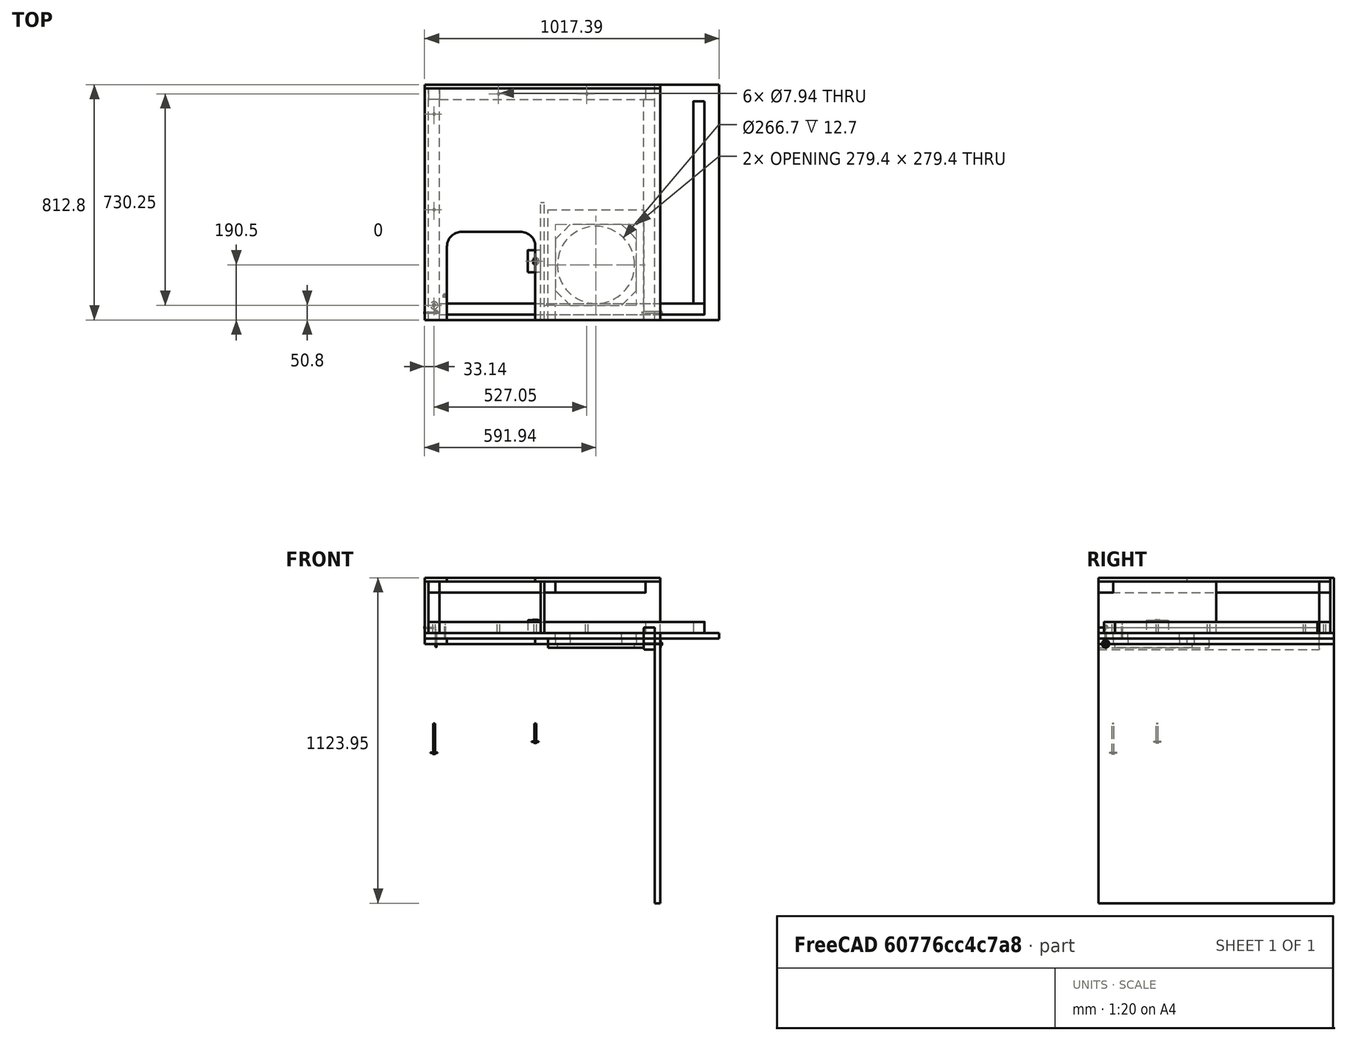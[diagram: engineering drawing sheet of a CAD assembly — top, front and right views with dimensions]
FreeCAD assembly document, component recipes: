
FREECAD ASSEMBLY — COMPONENT RECIPES ("Assembly")

This assembly document has 114 components, labeled P0..P113 below (a component is one placed body or linked part). 0 of them carry a construction recipe — the FreeCAD feature program that regenerates the part from scratch, quoted from this document or its linked companion documents; the rest are supplied as boundary geometry only. No exploded tour is included for this assembly.
COMPONENT P0 — geometry summary ("IF_A001"; no construction recipe available for this part):
  bounding box: 762.0 x 38.1 x 38.1 mm
  tessellated surface: 108 triangles
  volume: 1099533 mm^3 (99% of its bounding box)
  symmetry: 2-fold rotationally symmetric about the x axis; 4-fold rotationally symmetric about the y axis; 2-fold rotationally symmetric about the z axis; mirror-symmetric across its x mid-plane, z mid-plane
COMPONENT P1 — geometry summary ("Screw_w_Washer_B006"; no construction recipe available for this part):
  bounding box: 50.8 x 15.9 x 15.8 mm
  tessellated surface: 1,084 triangles
  volume: 650 mm^3 (5% of its bounding box)
  symmetry: 4-fold rotationally symmetric about the z axis; mirror-symmetric across its x mid-plane, y mid-plane
COMPONENT P2 — geometry summary ("Screw_w_Washer_B007"; no construction recipe available for this part):
  bounding box: 50.8 x 15.9 x 15.8 mm
  tessellated surface: 1,084 triangles
  volume: 650 mm^3 (5% of its bounding box)
  symmetry: 4-fold rotationally symmetric about the z axis; mirror-symmetric across its x mid-plane, y mid-plane
COMPONENT P3 — geometry summary ("Screw_w_Washer_B008"; no construction recipe available for this part):
  bounding box: 50.8 x 15.9 x 15.8 mm
  tessellated surface: 1,084 triangles
  volume: 650 mm^3 (5% of its bounding box)
  symmetry: 4-fold rotationally symmetric about the z axis; mirror-symmetric across its x mid-plane, y mid-plane
COMPONENT P4 — geometry summary ("Screw_w_Washer_B009"; no construction recipe available for this part):
  bounding box: 50.8 x 15.9 x 15.8 mm
  tessellated surface: 1,084 triangles
  volume: 650 mm^3 (5% of its bounding box)
  symmetry: 4-fold rotationally symmetric about the z axis; mirror-symmetric across its x mid-plane, y mid-plane
COMPONENT P5 — geometry summary ("Screw_w_Washer_B010"; no construction recipe available for this part):
  bounding box: 50.8 x 15.9 x 15.8 mm
  tessellated surface: 1,084 triangles
  volume: 650 mm^3 (5% of its bounding box)
  symmetry: 4-fold rotationally symmetric about the z axis; mirror-symmetric across its x mid-plane, y mid-plane
COMPONENT P6 — geometry summary ("Screw_w_Washer_B011"; no construction recipe available for this part):
  bounding box: 50.8 x 15.9 x 15.8 mm
  tessellated surface: 1,084 triangles
  volume: 650 mm^3 (5% of its bounding box)
  symmetry: 4-fold rotationally symmetric about the z axis; mirror-symmetric across its x mid-plane, y mid-plane
COMPONENT P7 — geometry summary ("Screw_w_Washer_B012"; no construction recipe available for this part):
  bounding box: 50.8 x 15.9 x 15.8 mm
  tessellated surface: 1,084 triangles
  volume: 650 mm^3 (5% of its bounding box)
  symmetry: 4-fold rotationally symmetric about the z axis; mirror-symmetric across its x mid-plane, y mid-plane
COMPONENT P8 — geometry summary ("Screw_w_Washer_B013"; no construction recipe available for this part):
  bounding box: 50.8 x 15.9 x 15.8 mm
  tessellated surface: 1,084 triangles
  volume: 650 mm^3 (5% of its bounding box)
  symmetry: 4-fold rotationally symmetric about the z axis; mirror-symmetric across its x mid-plane, y mid-plane
COMPONENT P9 — geometry summary ("Screw_w_Washer_B014"; no construction recipe available for this part):
  bounding box: 50.8 x 15.9 x 15.8 mm
  tessellated surface: 1,084 triangles
  volume: 650 mm^3 (5% of its bounding box)
  symmetry: 4-fold rotationally symmetric about the z axis; mirror-symmetric across its x mid-plane, y mid-plane
COMPONENT P10 — geometry summary ("Screw_w_Washer_B015"; no construction recipe available for this part):
  bounding box: 50.8 x 15.9 x 15.8 mm
  tessellated surface: 1,084 triangles
  volume: 650 mm^3 (5% of its bounding box)
  symmetry: 4-fold rotationally symmetric about the z axis; mirror-symmetric across its x mid-plane, y mid-plane
COMPONENT P11 — geometry summary ("Screw_w_Washer_B016"; no construction recipe available for this part):
  bounding box: 50.8 x 15.9 x 15.8 mm
  tessellated surface: 1,084 triangles
  volume: 650 mm^3 (5% of its bounding box)
  symmetry: 4-fold rotationally symmetric about the z axis; mirror-symmetric across its x mid-plane, y mid-plane
COMPONENT P12 — geometry summary ("Screw_w_Washer_B017"; no construction recipe available for this part):
  bounding box: 50.8 x 15.9 x 15.8 mm
  tessellated surface: 1,084 triangles
  volume: 650 mm^3 (5% of its bounding box)
  symmetry: 4-fold rotationally symmetric about the z axis; mirror-symmetric across its x mid-plane, y mid-plane
COMPONENT P13 — geometry summary ("Screw_w_Washer_B018"; no construction recipe available for this part):
  bounding box: 50.8 x 15.9 x 15.8 mm
  tessellated surface: 1,084 triangles
  volume: 650 mm^3 (5% of its bounding box)
  symmetry: 4-fold rotationally symmetric about the z axis; mirror-symmetric across its x mid-plane, y mid-plane
COMPONENT P14 — geometry summary ("Screw_w_Washer_B019"; no construction recipe available for this part):
  bounding box: 50.8 x 15.9 x 15.8 mm
  tessellated surface: 1,084 triangles
  volume: 650 mm^3 (5% of its bounding box)
  symmetry: 4-fold rotationally symmetric about the z axis; mirror-symmetric across its x mid-plane, y mid-plane
COMPONENT P15 — geometry summary ("Part_F_Baffle_Side_Wall_002"; no construction recipe available for this part):
  bounding box: 800.1 x 177.8 x 12.7 mm
  tessellated surface: 12 triangles
  volume: 1806674 mm^3 (100% of its bounding box)
  symmetry: 2-fold rotationally symmetric about the x axis; 2-fold rotationally symmetric about the y axis; 2-fold rotationally symmetric about the z axis; mirror-symmetric across its x mid-plane, y mid-plane, z mid-plane
COMPONENT P16 — geometry summary ("BF_A001"; no construction recipe available for this part):
  bounding box: 800.1 x 38.1 x 38.1 mm
  tessellated surface: 108 triangles
  volume: 1154510 mm^3 (99% of its bounding box)
  symmetry: 2-fold rotationally symmetric about the x axis; 4-fold rotationally symmetric about the y axis; 2-fold rotationally symmetric about the z axis; mirror-symmetric across its x mid-plane, z mid-plane
COMPONENT P17 — geometry summary ("BF_B001"; no construction recipe available for this part):
  bounding box: 711.2 x 38.1 x 38.1 mm
  tessellated surface: 108 triangles
  volume: 1026231 mm^3 (99% of its bounding box)
  symmetry: 2-fold rotationally symmetric about the x axis; 2-fold rotationally symmetric about the y axis; 2-fold rotationally symmetric about the z axis; mirror-symmetric across its y mid-plane, z mid-plane
COMPONENT P18 — geometry summary ("BF_C001"; no construction recipe available for this part):
  bounding box: 139.7 x 38.1 x 38.1 mm
  tessellated surface: 108 triangles
  volume: 201581 mm^3 (99% of its bounding box)
  symmetry: 2-fold rotationally symmetric about the y axis; 4-fold rotationally symmetric about the z axis; mirror-symmetric across its x mid-plane, y mid-plane, z mid-plane
COMPONENT P19 — geometry summary ("BF_E001"; no construction recipe available for this part):
  bounding box: 50.8 x 38.1 x 38.1 mm
  tessellated surface: 108 triangles
  volume: 73302 mm^3 (99% of its bounding box)
  symmetry: 2-fold rotationally symmetric about the x axis; 2-fold rotationally symmetric about the y axis; 2-fold rotationally symmetric about the z axis
COMPONENT P20 — geometry summary ("Screw_w_Washer_A001"; no construction recipe available for this part):
  bounding box: 38.1 x 15.9 x 15.8 mm
  tessellated surface: 1,086 triangles
  volume: 527 mm^3 (5% of its bounding box)
  symmetry: 4-fold rotationally symmetric about the x axis; mirror-symmetric across its y mid-plane
COMPONENT P21 — geometry summary ("Screw_w_Washer_A002"; no construction recipe available for this part):
  bounding box: 38.1 x 15.9 x 15.8 mm
  tessellated surface: 1,086 triangles
  volume: 527 mm^3 (5% of its bounding box)
  symmetry: 4-fold rotationally symmetric about the x axis; mirror-symmetric across its y mid-plane
COMPONENT P22 — geometry summary ("Screw_w_Washer_A003"; no construction recipe available for this part):
  bounding box: 38.1 x 15.9 x 15.8 mm
  tessellated surface: 1,086 triangles
  volume: 527 mm^3 (5% of its bounding box)
  symmetry: 4-fold rotationally symmetric about the x axis; mirror-symmetric across its y mid-plane
COMPONENT P23 — geometry summary ("Screw_w_Washer_A004"; no construction recipe available for this part):
  bounding box: 38.1 x 15.9 x 15.8 mm
  tessellated surface: 1,086 triangles
  volume: 527 mm^3 (5% of its bounding box)
  symmetry: 4-fold rotationally symmetric about the x axis; mirror-symmetric across its y mid-plane
COMPONENT P24 — geometry summary ("Screw_w_Washer_A005"; no construction recipe available for this part):
  bounding box: 38.1 x 15.9 x 15.8 mm
  tessellated surface: 1,086 triangles
  volume: 527 mm^3 (5% of its bounding box)
  symmetry: 4-fold rotationally symmetric about the x axis; mirror-symmetric across its y mid-plane
COMPONENT P25 — geometry summary ("Screw_w_Washer_A006"; no construction recipe available for this part):
  bounding box: 38.1 x 15.9 x 15.8 mm
  tessellated surface: 1,086 triangles
  volume: 527 mm^3 (5% of its bounding box)
  symmetry: 4-fold rotationally symmetric about the x axis; mirror-symmetric across its y mid-plane
COMPONENT P26 — geometry summary ("Screw_w_Washer_A007"; no construction recipe available for this part):
  bounding box: 38.1 x 15.9 x 15.8 mm
  tessellated surface: 1,086 triangles
  volume: 527 mm^3 (5% of its bounding box)
  symmetry: 4-fold rotationally symmetric about the x axis; mirror-symmetric across its y mid-plane
COMPONENT P27 — geometry summary ("Screw_w_Washer_A008"; no construction recipe available for this part):
  bounding box: 38.1 x 15.9 x 15.8 mm
  tessellated surface: 1,086 triangles
  volume: 527 mm^3 (5% of its bounding box)
  symmetry: 4-fold rotationally symmetric about the x axis; mirror-symmetric across its y mid-plane
COMPONENT P28 — geometry summary ("Screw_w_Washer_A009"; no construction recipe available for this part):
  bounding box: 38.1 x 15.9 x 15.8 mm
  tessellated surface: 1,086 triangles
  volume: 527 mm^3 (5% of its bounding box)
  symmetry: 4-fold rotationally symmetric about the x axis; mirror-symmetric across its y mid-plane
COMPONENT P29 — geometry summary ("Screw_w_Washer_A010"; no construction recipe available for this part):
  bounding box: 38.1 x 15.9 x 15.8 mm
  tessellated surface: 1,086 triangles
  volume: 527 mm^3 (5% of its bounding box)
  symmetry: 4-fold rotationally symmetric about the x axis; mirror-symmetric across its y mid-plane
COMPONENT P30 — geometry summary ("Screw_w_Washer_A011"; no construction recipe available for this part):
  bounding box: 38.1 x 15.9 x 15.8 mm
  tessellated surface: 1,086 triangles
  volume: 527 mm^3 (5% of its bounding box)
  symmetry: 4-fold rotationally symmetric about the x axis; mirror-symmetric across its y mid-plane
COMPONENT P31 — geometry summary ("Screw_w_Washer_A012"; no construction recipe available for this part):
  bounding box: 38.1 x 15.9 x 15.8 mm
  tessellated surface: 1,086 triangles
  volume: 527 mm^3 (5% of its bounding box)
  symmetry: 4-fold rotationally symmetric about the x axis; mirror-symmetric across its y mid-plane
COMPONENT P32 — geometry summary ("Screw_w_Washer_A013"; no construction recipe available for this part):
  bounding box: 38.1 x 15.9 x 15.8 mm
  tessellated surface: 1,086 triangles
  volume: 527 mm^3 (5% of its bounding box)
  symmetry: 4-fold rotationally symmetric about the x axis; mirror-symmetric across its y mid-plane
COMPONENT P33 — geometry summary ("Screw_w_Washer_A014"; no construction recipe available for this part):
  bounding box: 38.1 x 15.9 x 15.8 mm
  tessellated surface: 1,086 triangles
  volume: 527 mm^3 (5% of its bounding box)
  symmetry: 4-fold rotationally symmetric about the x axis; mirror-symmetric across its y mid-plane
COMPONENT P34 — geometry summary ("Screw_w_Washer_A015"; no construction recipe available for this part):
  bounding box: 38.1 x 15.9 x 15.8 mm
  tessellated surface: 1,086 triangles
  volume: 527 mm^3 (5% of its bounding box)
  symmetry: 4-fold rotationally symmetric about the x axis; mirror-symmetric across its y mid-plane
COMPONENT P35 — geometry summary ("Screw_w_Washer_A016"; no construction recipe available for this part):
  bounding box: 38.1 x 15.9 x 15.8 mm
  tessellated surface: 1,086 triangles
  volume: 527 mm^3 (5% of its bounding box)
  symmetry: 4-fold rotationally symmetric about the x axis; mirror-symmetric across its y mid-plane
COMPONENT P36 — geometry summary ("Screw_w_Washer_A017"; no construction recipe available for this part):
  bounding box: 38.1 x 15.9 x 15.8 mm
  tessellated surface: 1,086 triangles
  volume: 527 mm^3 (5% of its bounding box)
  symmetry: 4-fold rotationally symmetric about the x axis; mirror-symmetric across its y mid-plane
COMPONENT P37 — geometry summary ("Screw_w_Washer_A018"; no construction recipe available for this part):
  bounding box: 38.1 x 15.9 x 15.8 mm
  tessellated surface: 1,086 triangles
  volume: 527 mm^3 (5% of its bounding box)
  symmetry: 4-fold rotationally symmetric about the x axis; mirror-symmetric across its y mid-plane
COMPONENT P38 — geometry summary ("Screw_w_Washer_A019"; no construction recipe available for this part):
  bounding box: 38.1 x 15.9 x 15.8 mm
  tessellated surface: 1,086 triangles
  volume: 527 mm^3 (5% of its bounding box)
  symmetry: 4-fold rotationally symmetric about the x axis; mirror-symmetric across its y mid-plane
COMPONENT P39 — geometry summary ("Screw_w_Washer_A020"; no construction recipe available for this part):
  bounding box: 38.1 x 15.9 x 15.8 mm
  tessellated surface: 1,086 triangles
  volume: 527 mm^3 (5% of its bounding box)
  symmetry: 4-fold rotationally symmetric about the x axis; mirror-symmetric across its y mid-plane
COMPONENT P40 — geometry summary ("Screw_w_Washer_A021"; no construction recipe available for this part):
  bounding box: 38.1 x 15.9 x 15.8 mm
  tessellated surface: 1,086 triangles
  volume: 527 mm^3 (5% of its bounding box)
  symmetry: 4-fold rotationally symmetric about the x axis; mirror-symmetric across its y mid-plane
COMPONENT P41 — geometry summary ("Screw_w_Washer_A022"; no construction recipe available for this part):
  bounding box: 38.1 x 15.9 x 15.8 mm
  tessellated surface: 1,086 triangles
  volume: 527 mm^3 (5% of its bounding box)
  symmetry: 4-fold rotationally symmetric about the x axis; mirror-symmetric across its y mid-plane
COMPONENT P42 — geometry summary ("Screw_w_Washer_A023"; no construction recipe available for this part):
  bounding box: 38.1 x 15.9 x 15.8 mm
  tessellated surface: 1,086 triangles
  volume: 527 mm^3 (5% of its bounding box)
  symmetry: 4-fold rotationally symmetric about the x axis; mirror-symmetric across its y mid-plane
COMPONENT P43 — geometry summary ("Screw_w_Washer_A024"; no construction recipe available for this part):
  bounding box: 38.1 x 15.9 x 15.8 mm
  tessellated surface: 1,086 triangles
  volume: 527 mm^3 (5% of its bounding box)
  symmetry: 4-fold rotationally symmetric about the x axis; mirror-symmetric across its y mid-plane
COMPONENT P44 — geometry summary ("Screw_w_Washer_A025"; no construction recipe available for this part):
  bounding box: 38.1 x 15.9 x 15.8 mm
  tessellated surface: 1,086 triangles
  volume: 527 mm^3 (5% of its bounding box)
  symmetry: 4-fold rotationally symmetric about the x axis; mirror-symmetric across its y mid-plane
COMPONENT P45 — geometry summary ("Screw_w_Washer_A026"; no construction recipe available for this part):
  bounding box: 38.1 x 15.9 x 15.8 mm
  tessellated surface: 1,086 triangles
  volume: 527 mm^3 (5% of its bounding box)
  symmetry: 4-fold rotationally symmetric about the x axis; mirror-symmetric across its y mid-plane
COMPONENT P46 — geometry summary ("Screw_w_Washer_A027"; no construction recipe available for this part):
  bounding box: 38.1 x 15.9 x 15.8 mm
  tessellated surface: 1,086 triangles
  volume: 527 mm^3 (5% of its bounding box)
  symmetry: 4-fold rotationally symmetric about the x axis; mirror-symmetric across its y mid-plane
COMPONENT P47 — geometry summary ("Screw_w_Washer_A028"; no construction recipe available for this part):
  bounding box: 38.1 x 15.9 x 15.8 mm
  tessellated surface: 1,086 triangles
  volume: 527 mm^3 (5% of its bounding box)
  symmetry: 4-fold rotationally symmetric about the x axis; mirror-symmetric across its y mid-plane
COMPONENT P48 — geometry summary ("Screw_w_Washer_A029"; no construction recipe available for this part):
  bounding box: 38.1 x 15.9 x 15.8 mm
  tessellated surface: 1,086 triangles
  volume: 527 mm^3 (5% of its bounding box)
  symmetry: 4-fold rotationally symmetric about the x axis; mirror-symmetric across its y mid-plane
COMPONENT P49 — geometry summary ("Screw_w_Washer_A030"; no construction recipe available for this part):
  bounding box: 38.1 x 15.9 x 15.8 mm
  tessellated surface: 1,086 triangles
  volume: 527 mm^3 (5% of its bounding box)
  symmetry: 4-fold rotationally symmetric about the x axis; mirror-symmetric across its y mid-plane
COMPONENT P50 — geometry summary ("Screw_w_Washer_A031"; no construction recipe available for this part):
  bounding box: 38.1 x 15.9 x 15.8 mm
  tessellated surface: 1,086 triangles
  volume: 527 mm^3 (5% of its bounding box)
  symmetry: 4-fold rotationally symmetric about the x axis; mirror-symmetric across its y mid-plane
COMPONENT P51 — geometry summary ("Screw_w_Washer_A032"; no construction recipe available for this part):
  bounding box: 38.1 x 15.9 x 15.8 mm
  tessellated surface: 1,086 triangles
  volume: 527 mm^3 (5% of its bounding box)
  symmetry: 4-fold rotationally symmetric about the x axis; mirror-symmetric across its y mid-plane
COMPONENT P52 — geometry summary ("Screw_w_Washer_A033"; no construction recipe available for this part):
  bounding box: 38.1 x 15.9 x 15.8 mm
  tessellated surface: 1,086 triangles
  volume: 527 mm^3 (5% of its bounding box)
  symmetry: 4-fold rotationally symmetric about the x axis; mirror-symmetric across its y mid-plane
COMPONENT P53 — geometry summary ("Screw_w_Washer_A034"; no construction recipe available for this part):
  bounding box: 38.1 x 15.9 x 15.8 mm
  tessellated surface: 1,086 triangles
  volume: 527 mm^3 (5% of its bounding box)
  symmetry: 4-fold rotationally symmetric about the x axis; mirror-symmetric across its y mid-plane
COMPONENT P54 — geometry summary ("Screw_w_Washer_A035"; no construction recipe available for this part):
  bounding box: 38.1 x 15.9 x 15.8 mm
  tessellated surface: 1,086 triangles
  volume: 527 mm^3 (5% of its bounding box)
  symmetry: 4-fold rotationally symmetric about the x axis; mirror-symmetric across its y mid-plane
COMPONENT P55 — geometry summary ("Screw_w_Washer_A036"; no construction recipe available for this part):
  bounding box: 38.1 x 15.9 x 15.8 mm
  tessellated surface: 1,086 triangles
  volume: 527 mm^3 (5% of its bounding box)
  symmetry: 4-fold rotationally symmetric about the x axis; mirror-symmetric across its y mid-plane
COMPONENT P56 — geometry summary ("Screw_w_Washer_A037"; no construction recipe available for this part):
  bounding box: 38.1 x 15.9 x 15.8 mm
  tessellated surface: 1,086 triangles
  volume: 527 mm^3 (5% of its bounding box)
  symmetry: 4-fold rotationally symmetric about the x axis; mirror-symmetric across its y mid-plane
COMPONENT P57 — geometry summary ("Screw_w_Washer_A038"; no construction recipe available for this part):
  bounding box: 38.1 x 15.9 x 15.8 mm
  tessellated surface: 1,086 triangles
  volume: 527 mm^3 (5% of its bounding box)
  symmetry: 4-fold rotationally symmetric about the x axis; mirror-symmetric across its y mid-plane
COMPONENT P58 — geometry summary ("Screw_w_Washer_A039"; no construction recipe available for this part):
  bounding box: 38.1 x 15.9 x 15.8 mm
  tessellated surface: 1,086 triangles
  volume: 527 mm^3 (5% of its bounding box)
  symmetry: 4-fold rotationally symmetric about the x axis; mirror-symmetric across its y mid-plane
COMPONENT P59 — geometry summary ("Screw_w_Washer_A040"; no construction recipe available for this part):
  bounding box: 38.1 x 15.9 x 15.8 mm
  tessellated surface: 1,086 triangles
  volume: 527 mm^3 (5% of its bounding box)
  symmetry: 4-fold rotationally symmetric about the x axis; mirror-symmetric across its y mid-plane
COMPONENT P60 — geometry summary ("Screw_w_Washer_A041"; no construction recipe available for this part):
  bounding box: 38.1 x 15.9 x 15.8 mm
  tessellated surface: 1,086 triangles
  volume: 527 mm^3 (5% of its bounding box)
  symmetry: 4-fold rotationally symmetric about the x axis; mirror-symmetric across its y mid-plane
COMPONENT P61 — geometry summary ("Screw_w_Washer_A042"; no construction recipe available for this part):
  bounding box: 38.1 x 15.9 x 15.8 mm
  tessellated surface: 1,086 triangles
  volume: 527 mm^3 (5% of its bounding box)
  symmetry: 4-fold rotationally symmetric about the x axis; mirror-symmetric across its y mid-plane
COMPONENT P62 — geometry summary ("Screw_w_Washer_A043"; no construction recipe available for this part):
  bounding box: 38.1 x 15.9 x 15.8 mm
  tessellated surface: 1,086 triangles
  volume: 527 mm^3 (5% of its bounding box)
  symmetry: 4-fold rotationally symmetric about the x axis; mirror-symmetric across its y mid-plane
COMPONENT P63 — geometry summary ("Screw_w_Washer_A044"; no construction recipe available for this part):
  bounding box: 38.1 x 15.9 x 15.8 mm
  tessellated surface: 1,086 triangles
  volume: 527 mm^3 (5% of its bounding box)
  symmetry: 4-fold rotationally symmetric about the x axis; mirror-symmetric across its y mid-plane
COMPONENT P64 — geometry summary ("Screw_w_Washer_A045"; no construction recipe available for this part):
  bounding box: 38.1 x 15.9 x 15.8 mm
  tessellated surface: 1,086 triangles
  volume: 527 mm^3 (5% of its bounding box)
  symmetry: 4-fold rotationally symmetric about the x axis; mirror-symmetric across its y mid-plane
COMPONENT P65 — geometry summary ("Screw_w_Washer_A046"; no construction recipe available for this part):
  bounding box: 38.1 x 15.9 x 15.8 mm
  tessellated surface: 1,086 triangles
  volume: 527 mm^3 (5% of its bounding box)
  symmetry: 4-fold rotationally symmetric about the x axis; mirror-symmetric across its y mid-plane
COMPONENT P66 — geometry summary ("Cylinder001"; no construction recipe available for this part):
  bounding box: 50.8 x 7.9 x 7.9 mm
  tessellated surface: 104 triangles
  volume: 2514 mm^3 (79% of its bounding box)
  symmetry: 2-fold rotationally symmetric about the y axis; 6-fold rotationally symmetric about the z axis; mirror-symmetric across its x mid-plane, y mid-plane, z mid-plane
COMPONENT P67 — geometry summary ("Cylinder002"; no construction recipe available for this part):
  bounding box: 50.8 x 7.9 x 7.9 mm
  tessellated surface: 104 triangles
  volume: 2514 mm^3 (79% of its bounding box)
  symmetry: 2-fold rotationally symmetric about the y axis; 6-fold rotationally symmetric about the z axis; mirror-symmetric across its x mid-plane, y mid-plane, z mid-plane
COMPONENT P68 — geometry summary ("Cylinder003"; no construction recipe available for this part):
  bounding box: 50.8 x 7.9 x 7.9 mm
  tessellated surface: 104 triangles
  volume: 2514 mm^3 (79% of its bounding box)
  symmetry: 2-fold rotationally symmetric about the y axis; 6-fold rotationally symmetric about the z axis; mirror-symmetric across its x mid-plane, y mid-plane, z mid-plane
COMPONENT P69 — geometry summary ("Baffle_Frame_D001"; no construction recipe available for this part):
  bounding box: 762.0 x 38.1 x 38.1 mm
  tessellated surface: 444 triangles
  volume: 1093877 mm^3 (99% of its bounding box)
  symmetry: 2-fold rotationally symmetric about the x axis; 2-fold rotationally symmetric about the z axis; mirror-symmetric across its x mid-plane, y mid-plane, z mid-plane
COMPONENT P70 — geometry summary ("T-Nut_1/005"; no construction recipe available for this part):
  bounding box: 18.0 x 18.0 x 9.0 mm
  tessellated surface: 764 triangles
  volume: 501 mm^3 (17% of its bounding box)
  symmetry: 4-fold rotationally symmetric about the z axis
COMPONENT P71 — geometry summary ("T-Nut_1/006"; no construction recipe available for this part):
  bounding box: 18.0 x 18.0 x 9.0 mm
  tessellated surface: 764 triangles
  volume: 501 mm^3 (17% of its bounding box)
  symmetry: 4-fold rotationally symmetric about the z axis
COMPONENT P72 — geometry summary ("T-Nut_1/007"; no construction recipe available for this part):
  bounding box: 18.0 x 18.0 x 9.0 mm
  tessellated surface: 764 triangles
  volume: 501 mm^3 (17% of its bounding box)
  symmetry: 4-fold rotationally symmetric about the z axis
COMPONENT P73 — geometry summary ("T-Nut_1/008"; no construction recipe available for this part):
  bounding box: 18.0 x 18.0 x 9.0 mm
  tessellated surface: 764 triangles
  volume: 501 mm^3 (17% of its bounding box)
  symmetry: 4-fold rotationally symmetric about the z axis
COMPONENT P74 — geometry summary ("T-Nut_1/009"; no construction recipe available for this part):
  bounding box: 18.0 x 18.0 x 9.0 mm
  tessellated surface: 764 triangles
  volume: 501 mm^3 (17% of its bounding box)
  symmetry: 4-fold rotationally symmetric about the z axis
COMPONENT P75 — geometry summary ("T-Nut_1/010"; no construction recipe available for this part):
  bounding box: 18.0 x 18.0 x 9.0 mm
  tessellated surface: 764 triangles
  volume: 501 mm^3 (17% of its bounding box)
  symmetry: 4-fold rotationally symmetric about the z axis
COMPONENT P76 — geometry summary ("Cylinder004"; no construction recipe available for this part):
  bounding box: 50.8 x 7.9 x 7.9 mm
  tessellated surface: 104 triangles
  volume: 2514 mm^3 (79% of its bounding box)
  symmetry: 2-fold rotationally symmetric about the y axis; 6-fold rotationally symmetric about the z axis; mirror-symmetric across its x mid-plane, y mid-plane, z mid-plane
COMPONENT P77 — geometry summary ("Cylinder005"; no construction recipe available for this part):
  bounding box: 50.8 x 7.9 x 7.9 mm
  tessellated surface: 104 triangles
  volume: 2514 mm^3 (79% of its bounding box)
  symmetry: 2-fold rotationally symmetric about the y axis; 6-fold rotationally symmetric about the z axis; mirror-symmetric across its x mid-plane, y mid-plane, z mid-plane
COMPONENT P78 — geometry summary ("T-Nut_1/011"; no construction recipe available for this part):
  bounding box: 18.0 x 18.0 x 9.0 mm
  tessellated surface: 764 triangles
  volume: 501 mm^3 (17% of its bounding box)
  symmetry: 4-fold rotationally symmetric about the z axis
COMPONENT P79 — geometry summary ("T-Nut_1/012"; no construction recipe available for this part):
  bounding box: 18.0 x 18.0 x 9.0 mm
  tessellated surface: 764 triangles
  volume: 501 mm^3 (17% of its bounding box)
  symmetry: 4-fold rotationally symmetric about the z axis
COMPONENT P80 — geometry summary ("Screw_w_Washer_A047"; no construction recipe available for this part):
  bounding box: 38.1 x 15.9 x 15.8 mm
  tessellated surface: 1,086 triangles
  volume: 527 mm^3 (5% of its bounding box)
  symmetry: 4-fold rotationally symmetric about the x axis; mirror-symmetric across its y mid-plane
COMPONENT P81 — geometry summary ("Screw_w_Washer_C004"; no construction recipe available for this part):
  bounding box: 106.1 x 25.4 x 25.4 mm
  tessellated surface: 2,056 triangles
  volume: 3809 mm^3 (6% of its bounding box)
  symmetry: 4-fold rotationally symmetric about the z axis; mirror-symmetric across its x mid-plane, y mid-plane
COMPONENT P82 — geometry summary ("Screw_w_Washer_C005"; no construction recipe available for this part):
  bounding box: 106.1 x 25.4 x 25.4 mm
  tessellated surface: 2,056 triangles
  volume: 3809 mm^3 (6% of its bounding box)
  symmetry: 4-fold rotationally symmetric about the z axis; mirror-symmetric across its x mid-plane, y mid-plane
COMPONENT P83 — geometry summary ("Screw_w_Washer_C006"; no construction recipe available for this part):
  bounding box: 106.1 x 25.4 x 25.4 mm
  tessellated surface: 2,056 triangles
  volume: 3809 mm^3 (6% of its bounding box)
  symmetry: 4-fold rotationally symmetric about the z axis; mirror-symmetric across its x mid-plane, y mid-plane
COMPONENT P84 — geometry summary ("Screw_w_Washer_D001"; no construction recipe available for this part):
  bounding box: 68.0 x 25.4 x 25.4 mm
  tessellated surface: 1,980 triangles
  volume: 2732 mm^3 (6% of its bounding box)
  symmetry: revolution-symmetric about the z axis through its bounding-box center; mirror-symmetric across its x mid-plane, y mid-plane
COMPONENT P85 — geometry summary ("Screw_w_Washer_D002"; no construction recipe available for this part):
  bounding box: 68.0 x 25.4 x 25.4 mm
  tessellated surface: 1,980 triangles
  volume: 2732 mm^3 (6% of its bounding box)
  symmetry: revolution-symmetric about the z axis through its bounding-box center; mirror-symmetric across its x mid-plane, y mid-plane
COMPONENT P86 — geometry summary ("LinkGroup_Baffle_Box_2"; no construction recipe available for this part):
  bounding box: 816.6 x 814.5 x 192.0 mm
  tessellated surface: 61,476 triangles
  volume: 20863479 mm^3 (16% of its bounding box)
COMPONENT P87 — geometry summary ("LinkGroup_Baffle_Anchor_Screws_2"; no construction recipe available for this part):
  bounding box: 774.7 x 755.6 x 106.1 mm
  tessellated surface: 18,276 triangles
  volume: 31052 mm^3 (0% of its bounding box)
COMPONENT P88 — geometry summary ("IF_A002"; no construction recipe available for this part):
  bounding box: 762.0 x 38.1 x 38.1 mm
  tessellated surface: 108 triangles
  volume: 1099533 mm^3 (99% of its bounding box)
  symmetry: 2-fold rotationally symmetric about the x axis; 4-fold rotationally symmetric about the y axis; 2-fold rotationally symmetric about the z axis; mirror-symmetric across its x mid-plane, z mid-plane
COMPONENT P89 — geometry summary ("Screw_w_Washer_B021"; no construction recipe available for this part):
  bounding box: 50.8 x 15.9 x 15.8 mm
  tessellated surface: 1,084 triangles
  volume: 650 mm^3 (5% of its bounding box)
  symmetry: 2-fold rotationally symmetric about the z axis; mirror-symmetric across its x mid-plane, y mid-plane
COMPONENT P90 — geometry summary ("Screw_w_Washer_B022"; no construction recipe available for this part):
  bounding box: 50.8 x 15.9 x 15.8 mm
  tessellated surface: 1,084 triangles
  volume: 650 mm^3 (5% of its bounding box)
  symmetry: 2-fold rotationally symmetric about the z axis; mirror-symmetric across its x mid-plane, y mid-plane
COMPONENT P91 — geometry summary ("Screw_w_Washer_B023"; no construction recipe available for this part):
  bounding box: 50.8 x 15.9 x 15.8 mm
  tessellated surface: 1,084 triangles
  volume: 650 mm^3 (5% of its bounding box)
  symmetry: 2-fold rotationally symmetric about the z axis; mirror-symmetric across its x mid-plane, y mid-plane
COMPONENT P92 — geometry summary ("Screw_w_Washer_B024"; no construction recipe available for this part):
  bounding box: 50.8 x 15.9 x 15.8 mm
  tessellated surface: 1,084 triangles
  volume: 650 mm^3 (5% of its bounding box)
  symmetry: 2-fold rotationally symmetric about the z axis; mirror-symmetric across its x mid-plane, y mid-plane
COMPONENT P93 — geometry summary ("Screw_w_Washer_B025"; no construction recipe available for this part):
  bounding box: 50.8 x 15.9 x 15.8 mm
  tessellated surface: 1,084 triangles
  volume: 650 mm^3 (5% of its bounding box)
  symmetry: 2-fold rotationally symmetric about the z axis; mirror-symmetric across its x mid-plane, y mid-plane
COMPONENT P94 — geometry summary ("Frame_Screws_A_LinkGroup001"; no construction recipe available for this part):
  bounding box: 727.0 x 50.8 x 15.9 mm
  tessellated surface: 6,504 triangles
  volume: 3897 mm^3 (1% of its bounding box)
  symmetry: 2-fold rotationally symmetric about the z axis; mirror-symmetric across its x mid-plane, y mid-plane
COMPONENT P95 — geometry summary ("Part_B_Side_Wall_002"; no construction recipe available for this part):
  bounding box: 914.4 x 812.8 x 19.1 mm
  tessellated surface: 12 triangles
  volume: 14158423 mm^3 (100% of its bounding box)
  symmetry: 2-fold rotationally symmetric about the x axis; 2-fold rotationally symmetric about the y axis; 2-fold rotationally symmetric about the z axis; mirror-symmetric across its x mid-plane, y mid-plane, z mid-plane
COMPONENT P96 — geometry summary ("LF_A001"; no construction recipe available for this part):
  bounding box: 914.4 x 38.1 x 38.1 mm
  tessellated surface: 108 triangles
  volume: 1319440 mm^3 (99% of its bounding box)
  symmetry: 4-fold rotationally symmetric about the x axis; 2-fold rotationally symmetric about the y axis; 2-fold rotationally symmetric about the z axis; mirror-symmetric across its x mid-plane, y mid-plane, z mid-plane
COMPONENT P97 — geometry summary ("LF_B001"; no construction recipe available for this part):
  bounding box: 698.5 x 38.1 x 38.1 mm
  tessellated surface: 108 triangles
  volume: 1007905 mm^3 (99% of its bounding box)
  symmetry: 2-fold rotationally symmetric about the x axis; 4-fold rotationally symmetric about the y axis; 2-fold rotationally symmetric about the z axis; mirror-symmetric across its x mid-plane, z mid-plane
COMPONENT P98 — geometry summary ("Screw_w_Washer_B032"; no construction recipe available for this part):
  bounding box: 50.8 x 15.9 x 15.8 mm
  tessellated surface: 1,084 triangles
  volume: 650 mm^3 (5% of its bounding box)
  symmetry: 2-fold rotationally symmetric about the z axis; mirror-symmetric across its x mid-plane, y mid-plane
COMPONENT P99 — geometry summary ("Screw_w_Washer_B033"; no construction recipe available for this part):
  bounding box: 50.8 x 15.9 x 15.8 mm
  tessellated surface: 1,084 triangles
  volume: 650 mm^3 (5% of its bounding box)
  symmetry: 2-fold rotationally symmetric about the z axis; mirror-symmetric across its x mid-plane, y mid-plane
COMPONENT P100 — geometry summary ("Screw_w_Washer_B034"; no construction recipe available for this part):
  bounding box: 50.8 x 15.9 x 15.8 mm
  tessellated surface: 1,084 triangles
  volume: 650 mm^3 (5% of its bounding box)
  symmetry: 2-fold rotationally symmetric about the z axis; mirror-symmetric across its x mid-plane, y mid-plane
COMPONENT P101 — geometry summary ("Screw_w_Washer_B035"; no construction recipe available for this part):
  bounding box: 50.8 x 15.9 x 15.8 mm
  tessellated surface: 1,084 triangles
  volume: 650 mm^3 (5% of its bounding box)
  symmetry: 2-fold rotationally symmetric about the z axis; mirror-symmetric across its x mid-plane, y mid-plane
COMPONENT P102 — geometry summary ("Screw_w_Washer_B036"; no construction recipe available for this part):
  bounding box: 50.8 x 15.9 x 15.8 mm
  tessellated surface: 1,084 triangles
  volume: 650 mm^3 (5% of its bounding box)
  symmetry: 2-fold rotationally symmetric about the z axis; mirror-symmetric across its x mid-plane, y mid-plane
COMPONENT P103 — geometry summary ("Screw_w_Washer_B037"; no construction recipe available for this part):
  bounding box: 50.8 x 15.9 x 15.8 mm
  tessellated surface: 1,084 triangles
  volume: 650 mm^3 (5% of its bounding box)
  symmetry: 2-fold rotationally symmetric about the z axis; mirror-symmetric across its x mid-plane, y mid-plane
COMPONENT P104 — geometry summary ("Screw_w_Washer_B045"; no construction recipe available for this part):
  bounding box: 50.8 x 15.9 x 15.8 mm
  tessellated surface: 1,084 triangles
  volume: 650 mm^3 (5% of its bounding box)
  symmetry: 2-fold rotationally symmetric about the z axis; mirror-symmetric across its x mid-plane, y mid-plane
COMPONENT P105 — geometry summary ("Screw_w_Washer_B046"; no construction recipe available for this part):
  bounding box: 50.8 x 15.9 x 15.8 mm
  tessellated surface: 1,084 triangles
  volume: 650 mm^3 (5% of its bounding box)
  symmetry: 2-fold rotationally symmetric about the z axis; mirror-symmetric across its x mid-plane, y mid-plane
COMPONENT P106 — geometry summary ("Screw_w_Washer_B047"; no construction recipe available for this part):
  bounding box: 50.8 x 15.9 x 15.8 mm
  tessellated surface: 1,084 triangles
  volume: 650 mm^3 (5% of its bounding box)
  symmetry: 2-fold rotationally symmetric about the z axis; mirror-symmetric across its x mid-plane, y mid-plane
COMPONENT P107 — geometry summary ("Screw_w_Washer_B048"; no construction recipe available for this part):
  bounding box: 50.8 x 15.9 x 15.8 mm
  tessellated surface: 1,084 triangles
  volume: 650 mm^3 (5% of its bounding box)
  symmetry: 2-fold rotationally symmetric about the z axis; mirror-symmetric across its x mid-plane, y mid-plane
COMPONENT P108 — geometry summary ("Screw_w_Washer_B049"; no construction recipe available for this part):
  bounding box: 50.8 x 15.9 x 15.8 mm
  tessellated surface: 1,084 triangles
  volume: 650 mm^3 (5% of its bounding box)
  symmetry: 2-fold rotationally symmetric about the z axis; mirror-symmetric across its x mid-plane, y mid-plane
COMPONENT P109 — geometry summary ("Screw_w_Washer_B050"; no construction recipe available for this part):
  bounding box: 50.8 x 15.9 x 15.8 mm
  tessellated surface: 1,084 triangles
  volume: 650 mm^3 (5% of its bounding box)
  symmetry: 2-fold rotationally symmetric about the z axis; mirror-symmetric across its x mid-plane, y mid-plane
COMPONENT P110 — geometry summary ("Screw_w_Washer_B051"; no construction recipe available for this part):
  bounding box: 50.8 x 15.9 x 15.8 mm
  tessellated surface: 1,084 triangles
  volume: 650 mm^3 (5% of its bounding box)
  symmetry: 2-fold rotationally symmetric about the z axis; mirror-symmetric across its x mid-plane, y mid-plane
COMPONENT P111 — geometry summary ("Screw_w_Washer_D006"; no construction recipe available for this part):
  bounding box: 68.0 x 25.4 x 25.4 mm
  tessellated surface: 1,980 triangles
  volume: 2732 mm^3 (6% of its bounding box)
  symmetry: 4-fold rotationally symmetric about the x axis; mirror-symmetric across its z mid-plane
COMPONENT P112 — geometry summary ("Screw_w_Washer_D007"; no construction recipe available for this part):
  bounding box: 68.0 x 25.4 x 25.4 mm
  tessellated surface: 1,980 triangles
  volume: 2732 mm^3 (6% of its bounding box)
  symmetry: 4-fold rotationally symmetric about the x axis; mirror-symmetric across its z mid-plane
COMPONENT P113 — geometry summary ("Screw_w_Washer_D008"; no construction recipe available for this part):
  bounding box: 68.0 x 25.4 x 25.4 mm
  tessellated surface: 1,980 triangles
  volume: 2732 mm^3 (6% of its bounding box)
  symmetry: 4-fold rotationally symmetric about the x axis; mirror-symmetric across its z mid-plane
PROVENANCE & LICENSES
A FreeCAD (.FCStd) document from a public repository crawl; recipes are the document's own serialized feature recipes (and, for linked parts, companion documents' recipes).
License: gpl-3.0.
